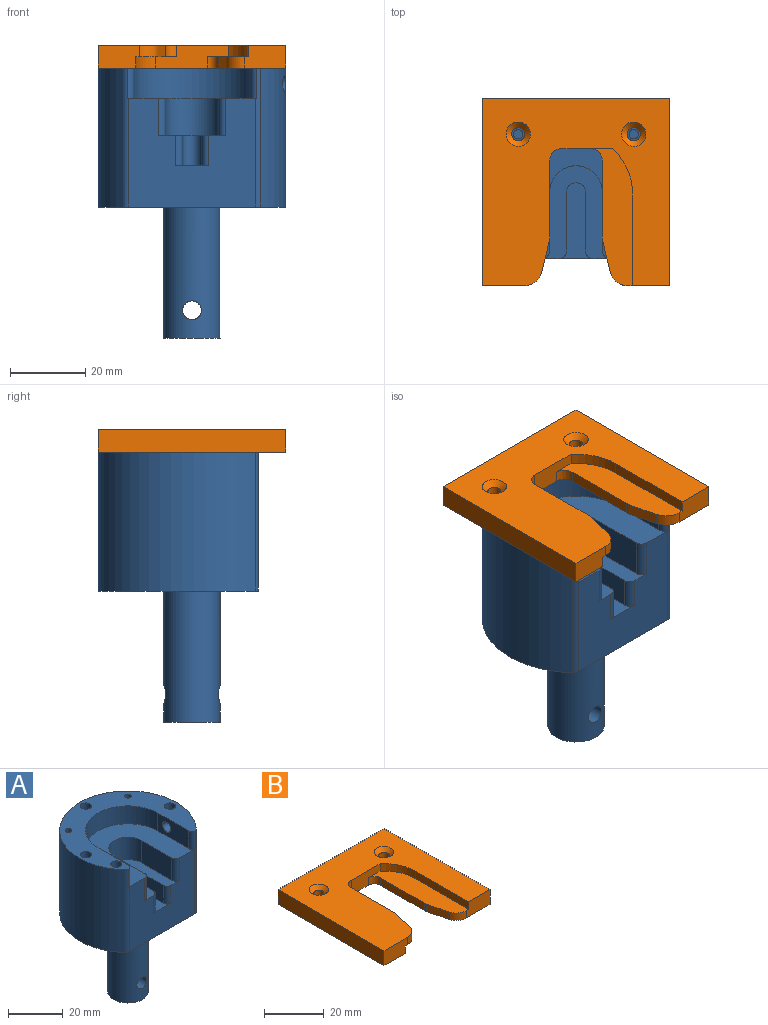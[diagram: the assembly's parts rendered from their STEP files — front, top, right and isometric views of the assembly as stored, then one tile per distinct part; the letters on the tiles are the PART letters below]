
ASSEMBLY  parts=2 mates=1
PART A: 40 faces, bbox 50x42.7x72 mm
  f0: plane 50x42.68mm, normal (0,0,-1), area 1609.4mm2, adj f2,f15,f30,f31,f33
  f1: plane 50x42.65mm, normal (0,0,1), area 797.8mm2, adj f2,f3,f4,f5,f6,f7,f8,f18
  f2: cylinder r=25mm len=50mm, axis (0,0,1), area 4278.7mm2, adj f0,f1,f31,f33,f39
  f3: cylinder r=2mm len=10mm, axis (0,0,1), area 125.7mm2, adj f1,f13
  f4: cylinder r=2mm len=10mm, axis (0,0,1), area 125.7mm2, adj f1,f9
  f5: cylinder r=1.25mm len=10mm, axis (0,0,1), area 78.5mm2, adj f1,f14
  f6: cylinder r=2mm len=10mm, axis (0,0,1), area 125.7mm2, adj f1,f12
  f7: cylinder r=1.25mm len=10mm, axis (0,0,1), area 78.5mm2, adj f1,f11
  f8: cylinder r=2mm len=10mm, axis (0,0,1), area 125.7mm2, adj f1,f10
  f9: plane 4x4mm, normal (0,0,1), area 12.6mm2, adj f4
  f10: plane 4x4mm, normal (0,0,1), area 12.6mm2, adj f8
  f11: plane 2.5x2.5mm, normal (0,0,1), area 4.9mm2, adj f7
  f12: plane 4x4mm, normal (0,0,1), area 12.6mm2, adj f6
  f13: plane 4x4mm, normal (0,0,1), area 12.6mm2, adj f3
  f14: plane 2.5x2.5mm, normal (0,0,1), area 4.9mm2, adj f5
  f15: cylinder r=7.47mm len=35mm, axis (0,0,-1), area 1604mm2, adj f0,f16,f17
  f16: plane 14.95x14.95mm, normal (0,0,-1), area 175.5mm2, adj f15
  f17: cylinder r=2.5mm len=14.95mm, axis (0,-1,0), area 228.1mm2, adj f15
  f18: plane 15.68x8mm, normal (-1,0,0), area 110.9mm2, adj f1,f19,f21,f32,f39
  f19: cylinder r=15.5mm len=31mm, axis (0,0,1), area 389.6mm2, adj f1,f18,f20,f21
  f20: plane 15.68x8mm, normal (1,0,0), area 125.4mm2, adj f1,f19,f21,f34
  f21: plane 34.33x33.18mm, normal (0,0,1), area 600.9mm2, adj f18,f19,f20,f22,f23,f24,f30,f31
  f22: plane 15.68x10mm, normal (-1,0,0), area 156.8mm2, adj f21,f23,f25,f35
  f23: cylinder r=7mm len=14mm, axis (0,0,1), area 219.9mm2, adj f21,f22,f24,f25
  f24: plane 15.68x10mm, normal (1,0,0), area 156.8mm2, adj f21,f23,f25,f36
  f25: plane 24.68x18mm, normal (0,0,1), area 226.3mm2, adj f22,f23,f24,f26,f27,f28,f30,f35
  f26: plane 15.68x8mm, normal (-1,0,0), area 125.4mm2, adj f25,f27,f29,f37
  f27: cylinder r=2.5mm len=8mm, axis (0,0,1), area 62.8mm2, adj f25,f26,f28,f29
  f28: plane 15.68x8mm, normal (1,0,0), area 125.4mm2, adj f25,f27,f29,f38
  f29: plane 20.18x9mm, normal (0,0,1), area 99.9mm2, adj f26,f27,f28,f30,f37,f38
  f30: plane 33.66x29mm, normal (0,-1,0), area 724.1mm2, adj f0,f21,f25,f29,f31,f33,f35,f36
  f31: cylinder r=2mm len=37mm, axis (0,0,1), area 58mm2, adj f0,f1,f2,f21,f30,f32
  f32: cylinder r=2mm len=8mm, axis (0,0,1), area 22.4mm2, adj f1,f18,f21,f31
  f33: cylinder r=2mm len=37mm, axis (0,0,1), area 58mm2, adj f0,f1,f2,f21,f30,f34
  f34: cylinder r=2mm len=8mm, axis (0,0,1), area 22.4mm2, adj f1,f20,f21,f33
  f35: cylinder r=2mm len=10mm, axis (0,0,1), area 31.4mm2, adj f21,f22,f25,f30
  f36: cylinder r=2mm len=10mm, axis (0,0,1), area 31.4mm2, adj f21,f24,f25,f30
  f37: cylinder r=2mm len=8mm, axis (0,0,1), area 25.1mm2, adj f25,f26,f29,f30
  f38: cylinder r=2mm len=8mm, axis (0,0,1), area 25.1mm2, adj f25,f28,f29,f30
  f39: cylinder r=2.15mm len=9.39mm, axis (-1,0,0), area 122.2mm2, adj f2,f18
PART B: 36 faces, bbox 50x50x6 mm
  f0: plane 11.06x6mm, normal (0,-1,0), area 63.2mm2, adj f1,f5,f9,f15,f33,f35
  f1: cylinder r=5mm len=4.86mm, axis (0,0,1), area 20mm2, adj f0,f5,f7,f35
  f2: cylinder r=5mm len=3mm, axis (0,0,-1), area 3.5mm2, adj f5,f7,f16,f35
  f3: plane 19.26x6mm, normal (0,-1,0), area 81.8mm2, adj f5,f6,f8,f9,f31,f32,f34,f35
  f4: plane 11.06x6mm, normal (0,-1,0), area 63.2mm2, adj f5,f9,f14,f17,f30,f32
  f5: plane 50x50mm, normal (0,0,-1), area 1626.5mm2, adj f0,f1,f2,f3,f4,f6,f7,f13
  f6: cylinder r=3mm len=3mm, axis (0,0,1), area 14.1mm2, adj f3,f5,f16,f35
  f7: plane 8.09x3mm, normal (-0.97,-0.23,0), area 25mm2, adj f1,f2,f5,f35
  f8: cylinder r=3mm len=3mm, axis (0,0,-1), area 14.1mm2, adj f3,f9,f11,f32
  f9: plane 50x50mm, normal (0,0,1), area 1629.6mm2, adj f0,f3,f4,f8,f10,f11,f12,f13
  f10: plane 8.09x3mm, normal (0.97,-0.23,0), area 25mm2, adj f9,f12,f17,f32
  f11: plane 20.41x3mm, normal (1,0,0), area 61.2mm2, adj f8,f9,f12,f32
  f12: cylinder r=5mm len=3mm, axis (0,0,-1), area 3.5mm2, adj f9,f10,f11,f32
  f13: plane 50x6mm, normal (0,1,0), area 300mm2, adj f5,f9,f14,f15
  f14: plane 50x6mm, normal (-1,0,0), area 300mm2, adj f4,f5,f9,f13
  f15: plane 50x6mm, normal (1,0,0), area 300mm2, adj f0,f5,f9,f13
  f16: plane 20.41x3mm, normal (-1,0,0), area 61.2mm2, adj f2,f5,f6,f35
  f17: cylinder r=5mm len=4.86mm, axis (0,0,-1), area 20mm2, adj f4,f9,f10,f32
  f18: cylinder r=1.75mm len=4.5mm, axis (0,0,-1), area 49.5mm2, adj f5,f28
  f19: cylinder r=1.75mm len=4.5mm, axis (0,0,-1), area 49.5mm2, adj f5,f29
  f20: cylinder r=2mm len=4mm, axis (0,0,-1), area 50.3mm2, adj f5,f21
  f21: plane 4x4mm, normal (0,0,-1), area 12.6mm2, adj f20
  f22: cylinder r=2mm len=4mm, axis (0,0,-1), area 50.3mm2, adj f5,f23
  f23: plane 4x4mm, normal (0,0,-1), area 12.6mm2, adj f22
  f24: cylinder r=2mm len=4mm, axis (0,0,-1), area 50.3mm2, adj f5,f25
  f25: plane 4x4mm, normal (0,0,-1), area 12.6mm2, adj f24
  f26: cylinder r=2mm len=4mm, axis (0,0,-1), area 50.3mm2, adj f5,f27
  f27: plane 4x4mm, normal (0,0,-1), area 12.6mm2, adj f26
  f28: cone r=1.75mm half-angle=45deg, axis (0,0,1), area 33.3mm2, adj f9,f18
  f29: cone r=1.75mm half-angle=45deg, axis (0,0,1), area 33.3mm2, adj f9,f19
  f30: plane 25x3mm, normal (1,0,0), area 75mm2, adj f4,f5,f31,f32
  f31: cylinder r=15mm len=11.5mm, axis (0,0,1), area 39.3mm2, adj f3,f5,f30,f32
  f32: plane 36.5x11mm, normal (0,0,-1), area 253.3mm2, adj f3,f4,f8,f10,f11,f12,f17,f30
  f33: plane 25x3mm, normal (-1,0,0), area 75mm2, adj f0,f9,f34,f35
  f34: cylinder r=15mm len=11.5mm, axis (0,0,-1), area 39.3mm2, adj f3,f9,f33,f35
  f35: plane 36.5x11mm, normal (0,0,1), area 253.3mm2, adj f0,f1,f2,f3,f6,f7,f16,f33
PLACE A t=(70.82,52.84,49.43)mm
PLACE B t=(70.82,52.84,59.43)mm
MATE fastened B.f26 <-> A.f6  axis (0,0,-1) through (70.82,74.59,59.43)mm
